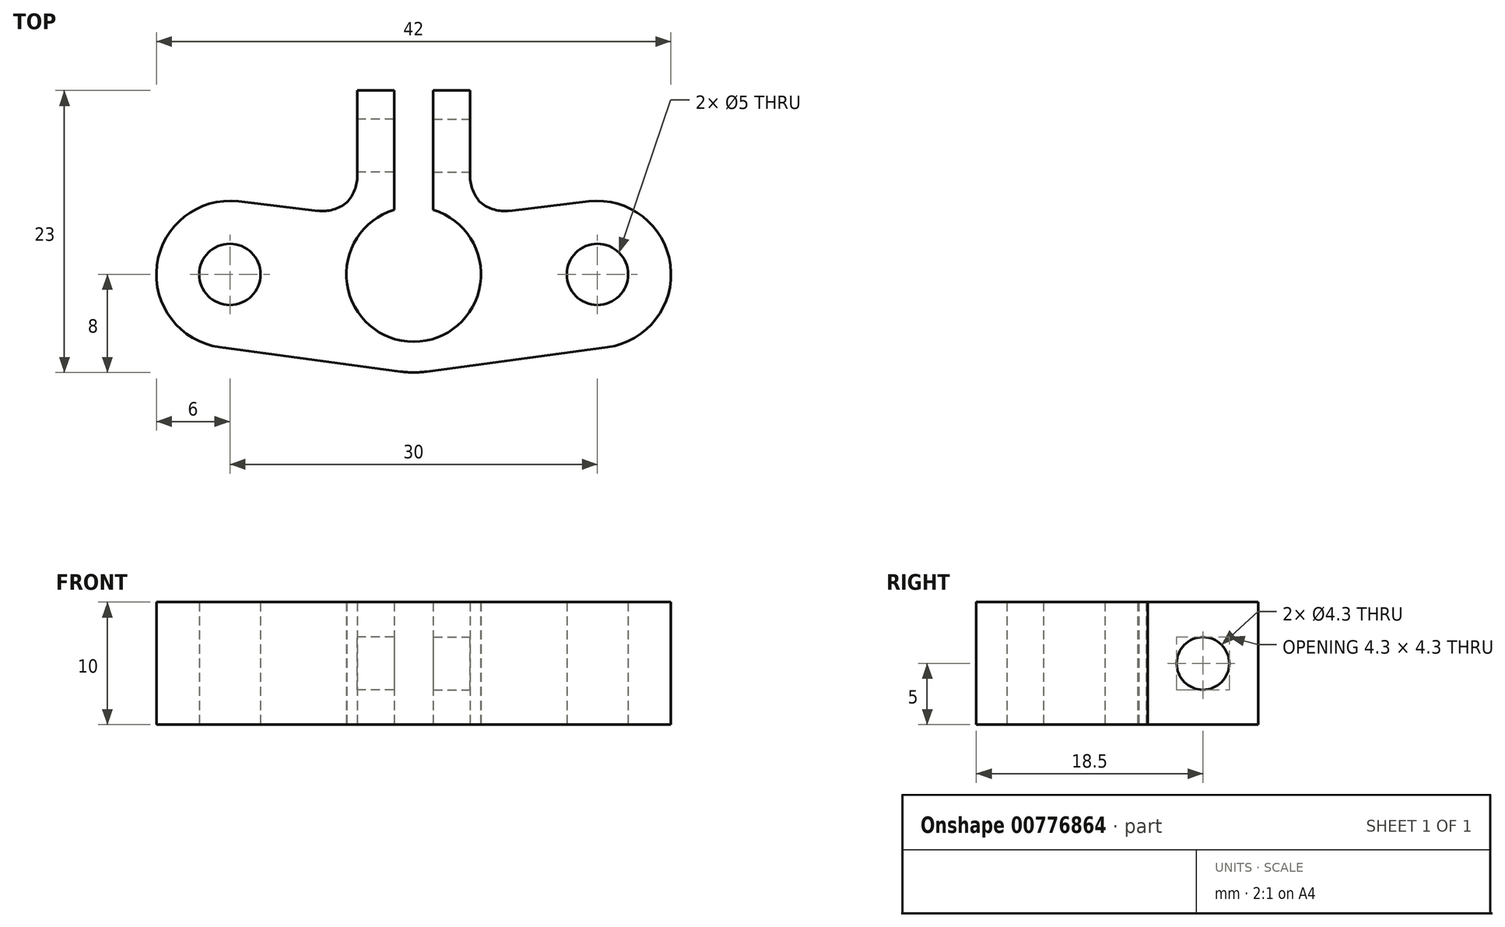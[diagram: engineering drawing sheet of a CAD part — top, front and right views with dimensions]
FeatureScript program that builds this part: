
annotation { "Feature Type Name" : "Feature", "Feature Type Description" : "" }
export const myFeature = defineFeature(function(context is Context, id is Id, definition is map)
    precondition{}
    {
        {
            var Q0;
            Q0=qCreatedBy(makeId("Top.planeOp"),FACE);
            var sketch = newSketch(context, id + "F0", { "sketchPlane" : qUnion([Q0])});
            skArc(sketch, "E0", {"start": v(0, -5.5) * mm, "mid": v(5.5, 0) * mm, "end": v(0, 5.5) * mm});
            skLineSegment(sketch, "E1", {"start": v(0, 0) * mm, "end": v(15, 0) * mm, "construction": true});
            skCircle(sketch, "E2", {"center": v(15, 0) * mm, "radius": 2.5 * mm});
            skArc(sketch, "E3", {"start": v(0, -8) * mm, "mid": v(8, 0) * mm, "end": v(0, 8) * mm});
            skLineSegment(sketch, "E4", {"start": v(0, 0) * mm, "end": v(0, 8) * mm, "construction": true});
            skLineSegment(sketch, "E5", {"start": v(0, 4.05) * mm, "end": v(1.6, 4.05) * mm, "construction": true});
            skLineSegment(sketch, "E6", {"start": v(1.6, 4.05) * mm, "end": v(1.6, 7.84) * mm});
            skLineSegment(sketch, "E7", {"start": v(1.6, 7.84) * mm, "end": v(1.6, 15) * mm});
            skLineSegment(sketch, "E8", {"start": v(1.6, 15) * mm, "end": v(4.6, 15) * mm});
            skLineSegment(sketch, "E9", {"start": v(4.6, 15) * mm, "end": v(4.6, 6.55) * mm});
            skCircle(sketch, "E10", {"center": v(15, 0) * mm, "radius": 6 * mm});
            skLineSegment(sketch, "E11", {"start": v(15.8, -5.95) * mm, "end": v(0, -8.07) * mm});
            skLineSegment(sketch, "E12", {"start": v(0, 0) * mm, "end": v(0, -8.07) * mm});
            skLineSegment(sketch, "E13", {"start": v(14.3, 5.96) * mm, "end": v(6.24, 5) * mm});
            skSolve(sketch);
        }
        {
            var Q0;
            {var subQ4=sQuery(id+"F0.wireOp",EDGE,"E12");var subQ5=sQuery(id+"F0.wireOp",EDGE,"E0");var subQ6=makeQuery(id+"F0.imprint","INTERSECT",VERTEX,{"derivedFrom":[subQ5,subQ4]});Q0=makeQuery(id+"F0.imprint","IMPRINT",FACE,{"disambiguationData":[TD([[makeQuery(id+"F0.imprint","IMPRINT",EDGE,{"disambiguationData":[TD([[subQ6,-1.0]])],"derivedFrom":subQ5}),-1.0]])]});}
            var Q1;
            {var subQ0=sQuery(id+"F0.wireOp",EDGE,"E13");Q1=makeQuery(id+"F0.imprint","IMPRINT",FACE,{"disambiguationData":[TD([[makeQuery(id+"F0.imprint","IMPRINT",EDGE,{"derivedFrom":subQ0}),1.0]])]});}
            var Q2;
            {var subQ0=sQuery(id+"F0.wireOp",EDGE,"E7");Q2=makeQuery(id+"F0.imprint","IMPRINT",FACE,{"disambiguationData":[TD([[makeQuery(id+"F0.imprint","IMPRINT",EDGE,{"derivedFrom":subQ0}),-1.0]])]});}
            var Q3;
            Q3=makeQuery(id+"F0.imprint","IMPRINT",FACE,{"disambiguationData":[TD([[makeQuery(id+"F0.imprint","IMPRINT",EDGE,{"derivedFrom":sQuery(id+"F0.wireOp",EDGE,"E2")}),-1.0]])]});
            extrude(context, id + "F1", {"entities" : qUnion([Q0, Q1, Q2, Q3]), "depth" : 10 * mm, "offsetDistance" : 25 * mm});
        }
        {
            var Q0;
            Q0=makeQuery(id+"F1.opExtrude","SWEPT_FACE",FACE,{"disambiguationData":[OSD([sQuery(id+"F0.wireOp",EDGE,"E9")])]});
            var sketch = newSketch(context, id + "F2", { "sketchPlane" : qUnion([Q0])});
            skCircle(sketch, "E14", {"center": v(10.5, 5) * mm, "radius": 2.15 * mm});
            skLineSegment(sketch, "E15", {"start": v(15, 5) * mm, "end": v(10.5, 5) * mm, "construction": true});
            skSolve(sketch);
        }
        {
            var Q0;
            Q0=qSketchRegion(id+"F2",true);
            extrude(context, id + "F3", {"entities" : qUnion([Q0]), "operationType" : NewBodyOperationType.REMOVE, "oppositeDirection" : true, "depth" : 25 * mm, "offsetDistance" : 25 * mm});
        }
        {
            var Q0;
            Q0=makeQuery(id+"F1.opExtrude","SWEPT_BODY",BODY,{"disambiguationData":[OSD([sQuery(id+"F0.wireOp",EDGE,"E0"),sQuery(id+"F0.wireOp",EDGE,"E2"),sQuery(id+"F0.wireOp",EDGE,"E3"),sQuery(id+"F0.wireOp",EDGE,"E6"),sQuery(id+"F0.wireOp",EDGE,"E7"),sQuery(id+"F0.wireOp",EDGE,"E8"),sQuery(id+"F0.wireOp",EDGE,"E9"),sQuery(id+"F0.wireOp",EDGE,"E10"),sQuery(id+"F0.wireOp",EDGE,"E11"),sQuery(id+"F0.wireOp",EDGE,"E12"),sQuery(id+"F0.wireOp",EDGE,"E13")])]});
            var Q1;
            Q1=qCreatedBy(makeId("Right.planeOp"),FACE);
            mirror(context, id + "F4", {"operationType" : NewBodyOperationType.ADD, "entities" : qUnion([Q0]), "mirrorPlane" : qUnion([Q1])});
        }
        {
            var Q0;
            Q0=makeQuery(id+"F4.opPattern","COPY",EDGE,{"derivedFrom":makeQuery(id+"F1.opExtrude","SWEPT_EDGE",EDGE,{"disambiguationData":[OSD([sQuery(id+"F0.wireOp",EDGE,"E3"),sQuery(id+"F0.wireOp",EDGE,"E9")])]}),"instanceName":"1"});
            var Q1;
            Q1=makeQuery(id+"F4.opPattern","COPY",EDGE,{"derivedFrom":makeQuery(id+"F1.opExtrude","SWEPT_EDGE",EDGE,{"disambiguationData":[OSD([sQuery(id+"F0.wireOp",EDGE,"E3"),sQuery(id+"F0.wireOp",EDGE,"E13")])]}),"instanceName":"1"});
            var Q2;
            Q2=makeQuery(id+"F1.opExtrude","SWEPT_EDGE",EDGE,{"disambiguationData":[OSD([sQuery(id+"F0.wireOp",EDGE,"E3"),sQuery(id+"F0.wireOp",EDGE,"E13")])]});
            var Q3;
            Q3=makeQuery(id+"F1.opExtrude","SWEPT_EDGE",EDGE,{"disambiguationData":[OSD([sQuery(id+"F0.wireOp",EDGE,"E3"),sQuery(id+"F0.wireOp",EDGE,"E9")])]});
            fillet(context, id + "F5", {"entities" : qUnion([Q0, Q1, Q2, Q3]), "radius" : 3.2 * mm, "tangentPropagation" : true, "allowEdgeOverflow" : false});
        }
    });
